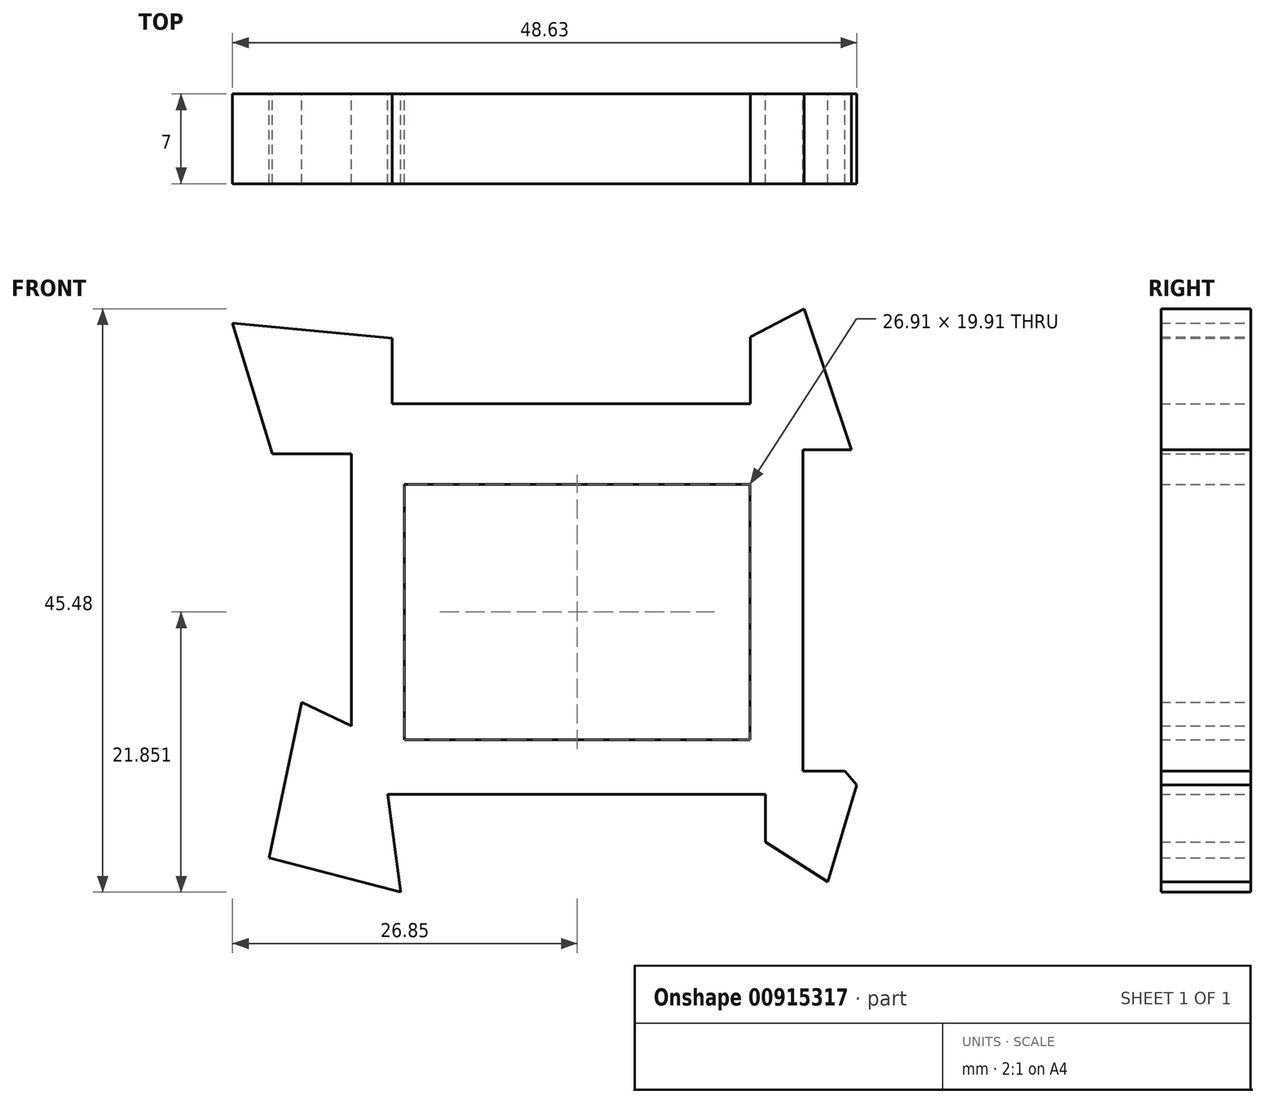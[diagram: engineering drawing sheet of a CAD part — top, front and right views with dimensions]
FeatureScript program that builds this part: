
annotation { "Feature Type Name" : "Feature", "Feature Type Description" : "" }
export const myFeature = defineFeature(function(context is Context, id is Id, definition is map)
    precondition{}
    {
        {
            var Q0;
            Q0=qCreatedBy(makeId("Front.planeOp"),FACE);
            var sketch = newSketch(context, id + "F0", { "sketchPlane" : qUnion([Q0])});
            skLineSegment(sketch, "E0", {"start": v(0, 8.95) * mm, "end": v(-13.45, 8.95) * mm});
            skLineSegment(sketch, "E1", {"start": v(-13.45, 8.95) * mm, "end": v(-13.45, -10.97) * mm});
            skLineSegment(sketch, "E2", {"start": v(-13.45, -10.97) * mm, "end": v(0, -10.97) * mm});
            skLineSegment(sketch, "E3.MirrorCS", {"start": v(0, 8.95) * mm, "end": v(13.45, 8.95) * mm});
            skLineSegment(sketch, "E4.MirrorCS", {"start": v(13.45, 8.95) * mm, "end": v(13.45, -10.97) * mm});
            skLineSegment(sketch, "E5.MirrorCS", {"start": v(13.45, -10.97) * mm, "end": v(0, -10.97) * mm});
            skLineSegment(sketch, "E6", {"start": v(0, 15.23) * mm, "end": v(-14.4, 15.23) * mm});
            skLineSegment(sketch, "E7", {"start": v(-17.6, 11.32) * mm, "end": v(-17.6, -9.88) * mm});
            skLineSegment(sketch, "E8", {"start": v(-14.76, -15.23) * mm, "end": v(0, -15.23) * mm});
            skLineSegment(sketch, "E9.MirrorCS", {"start": v(0, 15.23) * mm, "end": v(13.48, 15.23) * mm});
            skLineSegment(sketch, "E10.MirrorCS", {"start": v(17.6, 11.64) * mm, "end": v(17.6, -13.42) * mm});
            skLineSegment(sketch, "E11.MirrorCS", {"start": v(14.65, -15.23) * mm, "end": v(0, -15.23) * mm});
            skLineSegment(sketch, "E12", {"start": v(-14.4, 15.23) * mm, "end": v(-14.4, 20.33) * mm});
            skLineSegment(sketch, "E13", {"start": v(-17.6, 11.32) * mm, "end": v(-23.77, 11.32) * mm});
            skLineSegment(sketch, "E14", {"start": v(-23.77, 11.32) * mm, "end": v(-26.85, 21.51) * mm});
            skLineSegment(sketch, "E15", {"start": v(-26.85, 21.51) * mm, "end": v(-14.4, 20.33) * mm});
            skPoint(sketch, "E16.orphan", {"position": v(-17.6, 15.23) * mm});
            skLineSegment(sketch, "E17", {"start": v(-14.76, -15.23) * mm, "end": v(-13.75, -22.86) * mm});
            skLineSegment(sketch, "E18", {"start": v(-13.75, -22.86) * mm, "end": v(-24, -20.2) * mm});
            skLineSegment(sketch, "E19", {"start": v(-17.6, -9.88) * mm, "end": v(-21.45, -8.04) * mm});
            skLineSegment(sketch, "E20", {"start": v(-21.45, -8.04) * mm, "end": v(-24, -20.2) * mm});
            skPoint(sketch, "E21.orphan", {"position": v(-17.6, -15.23) * mm});
            skLineSegment(sketch, "E22", {"start": v(13.48, 15.23) * mm, "end": v(13.48, 20.44) * mm});
            skLineSegment(sketch, "E23", {"start": v(17.6, 11.64) * mm, "end": v(21.36, 11.64) * mm});
            skLineSegment(sketch, "E24", {"start": v(21.36, 11.64) * mm, "end": v(17.67, 22.62) * mm});
            skLineSegment(sketch, "E25", {"start": v(13.48, 20.44) * mm, "end": v(17.67, 22.62) * mm});
            skPoint(sketch, "E26.orphan", {"position": v(17.6, 15.23) * mm});
            skLineSegment(sketch, "E27", {"start": v(17.6, -13.42) * mm, "end": v(20.86, -13.42) * mm});
            skLineSegment(sketch, "E28", {"start": v(14.65, -15.23) * mm, "end": v(14.65, -18.95) * mm});
            skLineSegment(sketch, "E29", {"start": v(14.65, -18.95) * mm, "end": v(19.52, -22.06) * mm});
            skLineSegment(sketch, "E30", {"start": v(19.52, -22.06) * mm, "end": v(21.78, -14.51) * mm});
            skLineSegment(sketch, "E31", {"start": v(21.78, -14.51) * mm, "end": v(20.86, -13.42) * mm});
            skPoint(sketch, "E32.orphan", {"position": v(17.6, -15.23) * mm});
            skSolve(sketch);
        }
        {
            var Q0;
            Q0 = qSketchRegion(id + "F0", true);
            extrude(context, id + "F1", {"entities" : qUnion([Q0]), "depth" : 7 * mm, "offsetDistance" : 25.4 * mm});
        }
    });
